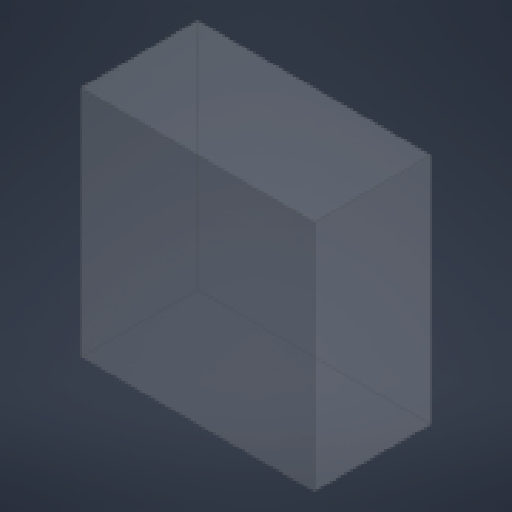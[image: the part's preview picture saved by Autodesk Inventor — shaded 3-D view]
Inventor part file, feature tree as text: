
AUTODESK INVENTOR PART (.ipt)
format: ipt  version: 2024.3 (Build 283343000, 343)  size: 113,152 bytes
history: native  units: mm
features: extrude x1, sketch x1
ambient origin geometry x8: Origin, YZ Plane, XZ Plane, XY Plane, X Axis, Y Axis, Z Axis, Center Point
bodies: Solid1 (feature_tree)
feature tree (2):
  extrude  "Extrusion1"  Depth=40.0mm TaperAngle=0.0deg
  sketch  "Sketch1"  dims[d0=80.0mm d1=40.0mm d2=0.0mm]
